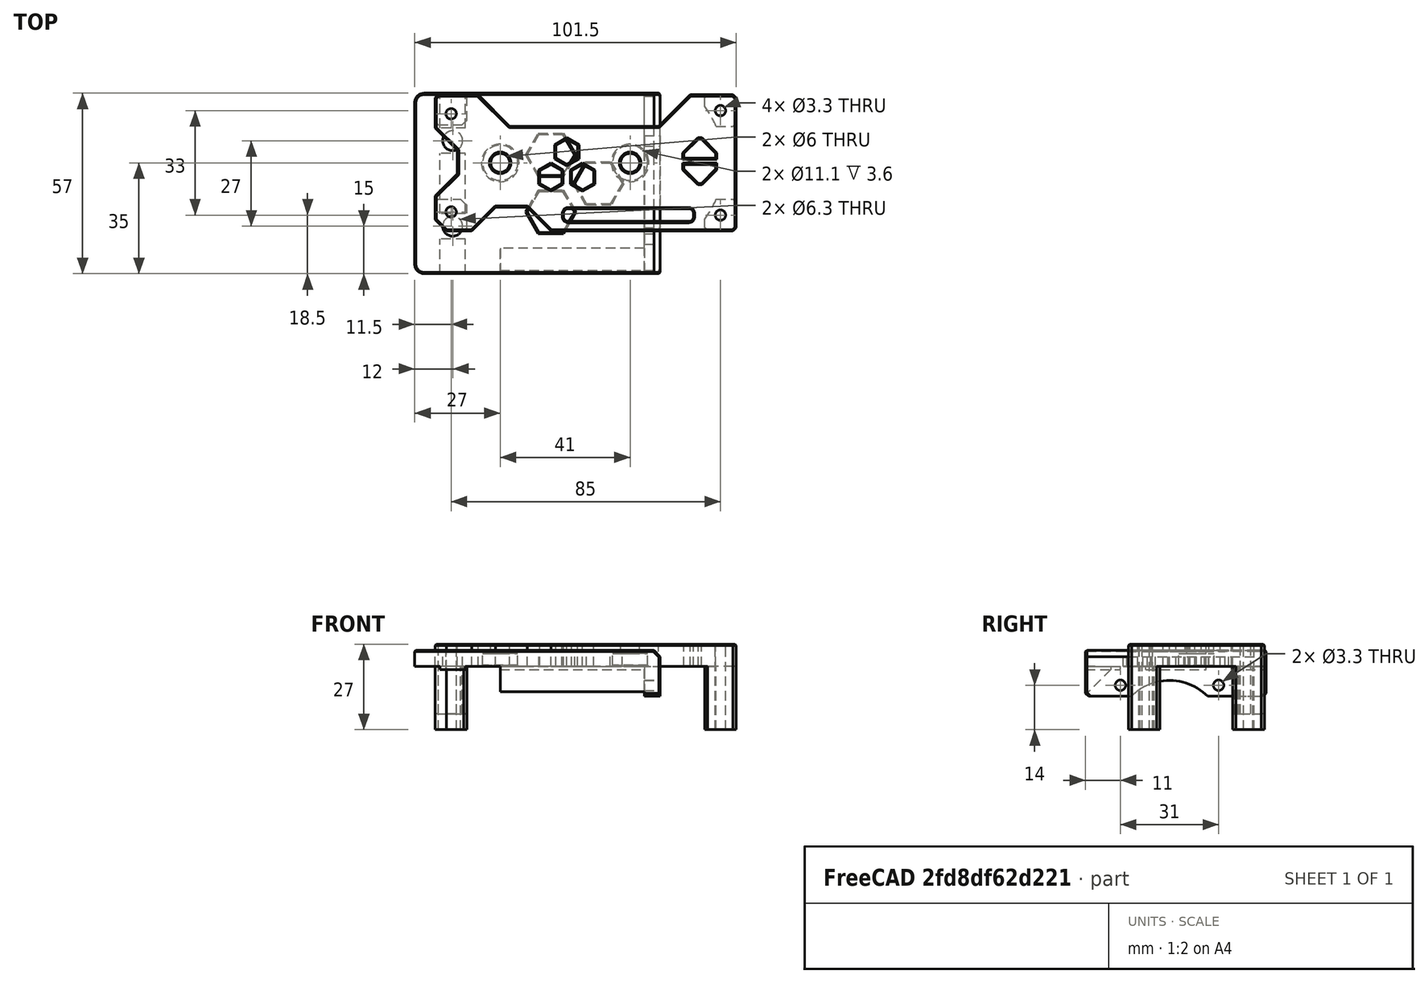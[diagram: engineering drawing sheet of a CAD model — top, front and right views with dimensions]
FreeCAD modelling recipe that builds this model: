
FCSTD DOCUMENT  (FreeCAD 0.18R16146 (Git))
Label: custom-gear-box-plate
License: Other
LicenseURL: GPL3
objects: Part::Feature×10, Part::Chamfer×6, Part::Box×6, Part::MultiFuse×4, Part::Cut×2, Part::Fillet×1
note: 29 computed .brp shape members not serialized (recipe doc carries the construction recipe); baked Part::Feature solids carry a one-line shape summary decoded from their .brp

FEATURE [Part::Feature] Chamfer029001  label="top-plate-r002"
  Placement = pos=(0,0,-30) rot=(0,0,1;0rad)
  shape: bbox 77.5 x 57 x 14.5 mm, 47 faces (baked)
FEATURE [Part::Feature] Cut001024006001  label="face-plate-plain001"
  Placement = pos=(1.45e-14,0,-65.5) rot=(-0.57735,-0.57735,-0.57735;2.0944rad)
  shape: bbox 95 x 43 x 27 mm, 48 faces (baked)
FEATURE [Part::Feature] Pad001001  label="Pad002"
  Placement = pos=(10,-1,0) rot=(0,0,1;4.71239rad)
  shape: bbox 15 x 12.99 x 10 mm, 8 faces (baked)
FEATURE [Part::Feature] Pad001002  label="Pad003"
  Placement = pos=(25,8,0) rot=(0,0,-1;1.5708rad)
  shape: bbox 15 x 12.99 x 10 mm, 8 faces (baked)
FEATURE [Part::Feature] Pad001003  label="Pad004"
  Placement = pos=(10,17,0) rot=(0,0,-1;1.5708rad)
  shape: bbox 15 x 12.99 x 10 mm, 8 faces (baked)
FEATURE [Part::MultiFuse] Fusion
  Placement = pos=(6,-6,0) rot=(0,0,1;0rad)
  Shapes = -> [Pad001001,Pad001002,Pad001003]
FEATURE [Part::Cut] Cut
  Base = -> Chamfer029001
  Tool = -> Fusion
FEATURE [Part::Chamfer] Chamfer  label="top-plate-type1"
  Base = -> Cut
  Edges = 18 edges r=0.4: [Edge7,Edge8,Edge9,Edge10,Edge11,Edge12,Edge13,Edge14,Edge15,Edge16,Edge17,Edge18,Edge19,Edge20,Edge21,Edge22,Edge23,Edge24]
FEATURE [Part::Box] Box  label="Cube"
  AttacherType = Attacher::AttachEngine3D
  Height = 10
  Length = 10
  Placement = pos=(58,10,0) rot=(0,0,1;0rad)
  Width = 6
FEATURE [Part::Box] Box001  label="Cube001"
  AttacherType = Attacher::AttachEngine3D
  Height = 10
  Length = 10
  Placement = pos=(58,2,0) rot=(0,0,1;0rad)
  Width = 6
FEATURE [Part::MultiFuse] Fusion001
  Shapes = -> [Box,Box001]
FEATURE [Part::Chamfer] Chamfer029002
  Base = -> Fusion001
  Edges = 4 edges r=4.5: [Edge3,Edge7,Edge13,Edge17]
FEATURE [Part::Box] Box002  label="Cube002"
  AttacherType = Attacher::AttachEngine3D
  Height = 10
  Length = 67
  Placement = pos=(-7,20,0) rot=(0,0,1;0rad)
  Width = 12
FEATURE [Part::Chamfer] Chamfer029003
  Base = -> Box002
  Edges = 2 edges r=10: [Edge1,Edge5]
FEATURE [Part::Box] Box004  label="Cube004"
  AttacherType = Attacher::AttachEngine3D
  Height = 10
  Length = 41
  Placement = pos=(20,-10,0) rot=(0,0,1;0rad)
  Width = 4
FEATURE [Part::Feature] Body003002001  label="Body003003"
  Placement = pos=(22,19,0) rot=(0,0,1;0rad)
  shape: bbox 6.928 x 8 x 10 mm, 8 faces (baked)
FEATURE [Part::Feature] Body003002002  label="Body003004"
  Placement = pos=(17,11,0) rot=(0,0,1;0rad)
  shape: bbox 6.928 x 8 x 10 mm, 8 faces (baked)
FEATURE [Part::Feature] Body003002003  label="Body003005"
  Placement = pos=(27,11,0) rot=(0,0,1;0rad)
  shape: bbox 6.928 x 8 x 10 mm, 8 faces (baked)
FEATURE [Part::MultiFuse] Fusion003
  Placement = pos=(-1,-7,0) rot=(0,0,1;0rad)
  Shapes = -> [Body003002003,Body003002002,Body003002001]
FEATURE [Part::Fillet] Fillet
  Base = -> Box004
  Edges = 4 edges r=1.5: [Edge1,Edge3,Edge5,Edge7]
FEATURE [Part::Box] Box005  label="Cube005"
  AttacherType = Attacher::AttachEngine3D
  Height = 10
  Length = 10
  Placement = pos=(-24,-2,0) rot=(0,0,1;0rad)
  Width = 21.5
FEATURE [Part::Chamfer] Chamfer029004
  Base = -> Box005
  Edges = 2 edges r=7: [Edge5,Edge7]
  Placement = pos=(0.5,0,0) rot=(0,0,1;0rad)
FEATURE [Part::Box] Box006  label="Cube006"
  AttacherType = Attacher::AttachEngine3D
  Height = 10
  Length = 25
  Placement = pos=(-9,-15.5,0) rot=(0,0,1;0rad)
  Width = 10
FEATURE [Part::Chamfer] Chamfer029005
  Base = -> Box006
  Edges = 2 edges r=7.5: [Edge3,Edge7]
FEATURE [Part::MultiFuse] Fusion004
  Shapes = -> [Chamfer029004,Chamfer029005,Fillet,Chamfer029003,Fusion003,Chamfer029002]
FEATURE [Part::Cut] Cut001024006002
  Base = -> Cut001024006001
  Tool = -> Fusion004
FEATURE [Part::Chamfer] Chamfer029006  label="front-plate-type1"
  Base = -> Cut001024006002
  Edges = 58 edges r=0.4: [Edge1,Edge2,Edge3,Edge4,Edge5,Edge6,Edge7,Edge8,Edge9,Edge10,Edge11,Edge12,Edge13,Edge14,Edge15,Edge16,Edge17,Edge18,Edge19,Edge20,Edge21,Edge22,Edge23,Edge24,Edge25,Edge26,Edge27,Edge28,Edge29,Edge30,Edge31,Edge32,Edge33,Edge34,Edge35,Edge36,Edge37,Edge38,Edge41,Edge42,Edge43,Edge44,Edge45,Edge46,+14 more]
FEATURE [Part::Feature] Chamfer029006001  label="front-plate-type001"
  shape: bbox 95 x 43 x 27 mm, 156 faces (baked)
FEATURE [Part::Feature] Chamfer029006002  label="top-plate-type001"
  shape: bbox 77.5 x 57 x 14.5 mm, 83 faces (baked)
